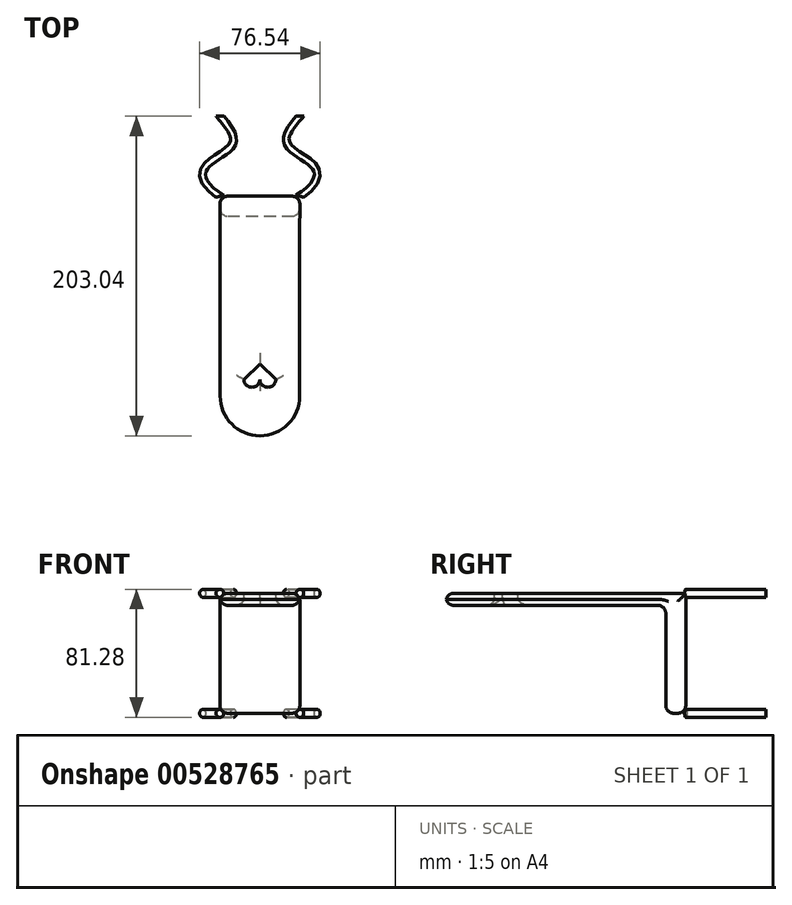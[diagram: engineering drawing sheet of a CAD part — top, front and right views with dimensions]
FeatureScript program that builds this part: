
annotation { "Feature Type Name" : "Feature", "Feature Type Description" : "" }
export const myFeature = defineFeature(function(context is Context, id is Id, definition is map)
    precondition{}
    {
        {
            var Q0;
            Q0=qCreatedBy(makeId("Front.planeOp"),FACE);
            var sketch = newSketch(context, id + "F0", { "sketchPlane" : qUnion([Q0])});
            skLineSegment(sketch, "E0.bottom", {"start": v(-50.8, 76.2) * mm, "end": v(0, 76.2) * mm});
            skLineSegment(sketch, "E0.top", {"start": v(-50.8, 0) * mm, "end": v(0, 0) * mm});
            skLineSegment(sketch, "E0.left", {"start": v(-50.8, 76.2) * mm, "end": v(-50.8, 0) * mm});
            skLineSegment(sketch, "E0.right", {"start": v(0, 76.2) * mm, "end": v(0, 0) * mm});
            skSolve(sketch);
        }
        {
            var Q0;
            Q0=makeQuery(id+"F0.imprint","IMPRINT",FACE,{"disambiguationData":[TD([[makeQuery(id+"F0.imprint","IMPRINT",EDGE,{"derivedFrom":sQuery(id+"F0.wireOp",EDGE,"E0.bottom")}),-1.0]])]});
            extrude(context, id + "F1", {"entities" : qUnion([Q0]), "depth" : 12.7 * mm, "offsetDistance" : 25.4 * mm});
        }
        {
            var Q0;
            Q0=qCreatedBy(makeId("Front.planeOp"),FACE);
            cPlane(context, id + "F2", {"entities" : qUnion([Q0]), "cplaneType" : CPlaneType.OFFSET, "offset" : 50.8 * mm, "oppositeDirection" : true, "width" : 152.4 * mm, "height" : 152.4 * mm});
        }
        {
            var Q0;
            Q0=qCreatedBy(id+"F2.planeOp",FACE);
            var sketch = newSketch(context, id + "F3", { "sketchPlane" : qUnion([Q0])});
            skCircle(sketch, "E1", {"center": v(0, 0) * mm, "radius": 2.54 * mm});
            skSolve(sketch);
        }
        {
            var Q0;
            Q0=makeQuery(id+"F1.opExtrude","SWEPT_FACE",FACE,{"disambiguationData":[OSD([sQuery(id+"F0.wireOp",EDGE,"E0.top")])]});
            var sketch = newSketch(context, id + "F4", { "sketchPlane" : qUnion([Q0])});
            skFitSpline(sketch, "E2", {"points": [v(0, 0) * mm, v(9.93, -17.42) * mm, v(-6.91, -31.62) * mm, v(0, -50.8) * mm], "startDerivative": vector(80.98, -50.96) * mm, "endDerivative": vector(72.85, -84.35) * mm});
            skSolve(sketch);
        }
        {
            var Q0;
            Q0=makeQuery(id+"F3.imprint","IMPRINT",FACE,{"disambiguationData":[TD([[makeQuery(id+"F3.imprint","IMPRINT",EDGE,{"derivedFrom":sQuery(id+"F3.wireOp",EDGE,"E1")}),1.0]])]});
            var Q1;
            Q1=sQuery(id+"F4.wireOp",EDGE,"E2");
            sweep(context, id + "F5", {"profiles" : qUnion([Q0]), "path" : qUnion([Q1])});
        }
        {
            var Q0;
            Q0=qCreatedBy(makeId("Right.planeOp"),FACE);
            cPlane(context, id + "F6", {"entities" : qUnion([Q0]), "cplaneType" : CPlaneType.OFFSET, "offset" : 25.4 * mm, "oppositeDirection" : true, "width" : 152.4 * mm, "height" : 152.4 * mm});
        }
        {
            var Q0;
            Q0=makeQuery(id+"F5.opSweep","SWEPT_BODY",BODY,{"disambiguationData":[OSD([sQuery(id+"F3.wireOp",EDGE,"E1"),sQuery(id+"F4.wireOp",EDGE,"E2")])]});
            var Q1;
            Q1=qCreatedBy(id+"F6.planeOp",FACE);
            mirror(context, id + "F7", {"entities" : qUnion([Q0]), "mirrorPlane" : qUnion([Q1])});
        }
        {
            var Q0;
            Q0=qCreatedBy(makeId("Top.planeOp"),FACE);
            cPlane(context, id + "F8", {"entities" : qUnion([Q0]), "cplaneType" : CPlaneType.OFFSET, "offset" : 38.1 * mm, "width" : 152.4 * mm, "height" : 152.4 * mm});
        }
        {
            var Q0;
            Q0=makeQuery(id+"F7.opPattern","COPY",BODY,{"derivedFrom":makeQuery(id+"F5.opSweep","SWEPT_BODY",BODY,{"disambiguationData":[OSD([sQuery(id+"F3.wireOp",EDGE,"E1"),sQuery(id+"F4.wireOp",EDGE,"E2")])]}),"instanceName":"1"});
            var Q1;
            Q1=makeQuery(id+"F5.opSweep","SWEPT_BODY",BODY,{"disambiguationData":[OSD([sQuery(id+"F3.wireOp",EDGE,"E1"),sQuery(id+"F4.wireOp",EDGE,"E2")])]});
            var Q2;
            Q2=qCreatedBy(id+"F8.planeOp",FACE);
            mirror(context, id + "F9", {"entities" : qUnion([Q0, Q1]), "mirrorPlane" : qUnion([Q2])});
        }
        {
            var Q0;
            Q0=makeQuery(id+"F1.opExtrude","SWEPT_FACE",FACE,{"disambiguationData":[OSD([sQuery(id+"F0.wireOp",EDGE,"E0.bottom")])]});
            var sketch = newSketch(context, id + "F10", { "sketchPlane" : qUnion([Q0])});
            skLineSegment(sketch, "E3.bottom", {"start": v(0, -12.7) * mm, "end": v(-50.8, -12.7) * mm});
            skLineSegment(sketch, "E3.left", {"start": v(0, -12.7) * mm, "end": v(0, -127) * mm});
            skLineSegment(sketch, "E3.right", {"start": v(-50.8, -12.7) * mm, "end": v(-50.8, -127) * mm});
            skArc(sketch, "E4", {"start": v(0, -127) * mm, "mid": v(-25.4, -152.4) * mm, "end": v(-50.8, -127) * mm});
            skSolve(sketch);
        }
        {
            var Q0;
            Q0=makeQuery(id+"F10.imprint","IMPRINT",FACE,{"disambiguationData":[TD([[makeQuery(id+"F10.imprint","IMPRINT",EDGE,{"derivedFrom":sQuery(id+"F10.wireOp",EDGE,"E3.bottom")}),-1.0]])]});
            extrude(context, id + "F11", {"entities" : qUnion([Q0]), "operationType" : NewBodyOperationType.ADD, "oppositeDirection" : true, "depth" : 7.62 * mm, "offsetDistance" : 25.4 * mm});
        }
        {
            var Q0;
            Q0=makeQuery(id+"F11.opExtrude","CAP_FACE",FACE,{"disambiguationData":[OSD([sQuery(id+"F10.wireOp",EDGE,"E3.bottom"),sQuery(id+"F10.wireOp",EDGE,"E3.left"),sQuery(id+"F10.wireOp",EDGE,"E3.right"),sQuery(id+"F10.wireOp",EDGE,"E4")])],"isStart":false});
            var Q1;
            Q1=makeQuery(id+"F1.opExtrude","SWEPT_FACE",FACE,{"disambiguationData":[OSD([sQuery(id+"F0.wireOp",EDGE,"E0.top")])]});
            var Q2;
            Q2=makeQuery(id+"F11.boolean.opBoolean","MERGE",FACE,{"derivedFrom":[makeQuery(id+"F1.opExtrude","SWEPT_FACE",FACE,{"disambiguationData":[OSD([sQuery(id+"F0.wireOp",EDGE,"E0.left")])]}),makeQuery(id+"F11.opExtrude","SWEPT_FACE",FACE,{"disambiguationData":[OSD([sQuery(id+"F10.wireOp",EDGE,"E3.right")])]})]});
            var Q3;
            Q3=makeQuery(id+"F11.boolean.opBoolean","MERGE",FACE,{"derivedFrom":[makeQuery(id+"F1.opExtrude","SWEPT_FACE",FACE,{"disambiguationData":[OSD([sQuery(id+"F0.wireOp",EDGE,"E0.right")])]}),makeQuery(id+"F11.opExtrude","SWEPT_FACE",FACE,{"disambiguationData":[OSD([sQuery(id+"F10.wireOp",EDGE,"E3.left")])]})]});
            fillet(context, id + "F12", {"entities" : qUnion([Q0, Q1, Q2, Q3]), "radius" : 5.08 * mm, "tangentPropagation" : true, "allowEdgeOverflow" : false});
        }
        {
            var Q0;
            Q0=makeQuery(id+"F11.boolean.opBoolean","MERGE",FACE,{"derivedFrom":[makeQuery(id+"F1.opExtrude","SWEPT_FACE",FACE,{"disambiguationData":[OSD([sQuery(id+"F0.wireOp",EDGE,"E0.bottom")])]}),makeQuery(id+"F11.opExtrude","CAP_FACE",FACE,{"disambiguationData":[OSD([sQuery(id+"F10.wireOp",EDGE,"E3.bottom"),sQuery(id+"F10.wireOp",EDGE,"E3.left"),sQuery(id+"F10.wireOp",EDGE,"E3.right"),sQuery(id+"F10.wireOp",EDGE,"E4")])],"isStart":true})]});
            var sketch = newSketch(context, id + "F13", { "sketchPlane" : qUnion([Q0])});
            skArc(sketch, "E5", {"start": v(-25.4, -116.32) * mm, "mid": v(-20.32, -121.4) * mm, "end": v(-15.24, -116.32) * mm});
            skLineSegment(sketch, "E6", {"start": v(-25.4, -147.32) * mm, "end": v(-25.4, 0) * mm, "construction": true});
            skArc(sketch, "E7.MirrorCS", {"start": v(-25.4, -116.32) * mm, "mid": v(-30.48, -121.4) * mm, "end": v(-35.56, -116.32) * mm});
            skLineSegment(sketch, "E8", {"start": v(-15.24, -116.32) * mm, "end": v(-25.4, -106.54) * mm});
            skLineSegment(sketch, "E9", {"start": v(-25.4, -106.54) * mm, "end": v(-35.56, -116.32) * mm});
            skCircle(sketch, "E10", {"center": v(-14.67, -69.83) * mm, "radius": 11.6 * mm, "construction": true});
            skSolve(sketch);
        }
        {
            var Q0;
            Q0 = qSketchRegion(id + "F13", true);
            extrude(context, id + "F14", {"entities" : qUnion([Q0]), "operationType" : NewBodyOperationType.REMOVE, "endBound" : BoundingType.THROUGH_ALL, "oppositeDirection" : true, "depth" : 25.4 * mm, "offsetDistance" : 25.4 * mm});
        }
        {
            var Q0;
            Q0=makeQuery(id+"F11.opExtrude","CAP_FACE",FACE,{"disambiguationData":[OSD([sQuery(id+"F10.wireOp",EDGE,"E3.bottom"),sQuery(id+"F10.wireOp",EDGE,"E3.left"),sQuery(id+"F10.wireOp",EDGE,"E3.right"),sQuery(id+"F10.wireOp",EDGE,"E4")])],"isStart":false});
            fillet(context, id + "F15", {"entities" : qUnion([Q0]), "radius" : 5.08 * mm, "tangentPropagation" : true, "allowEdgeOverflow" : false});
        }
    });
